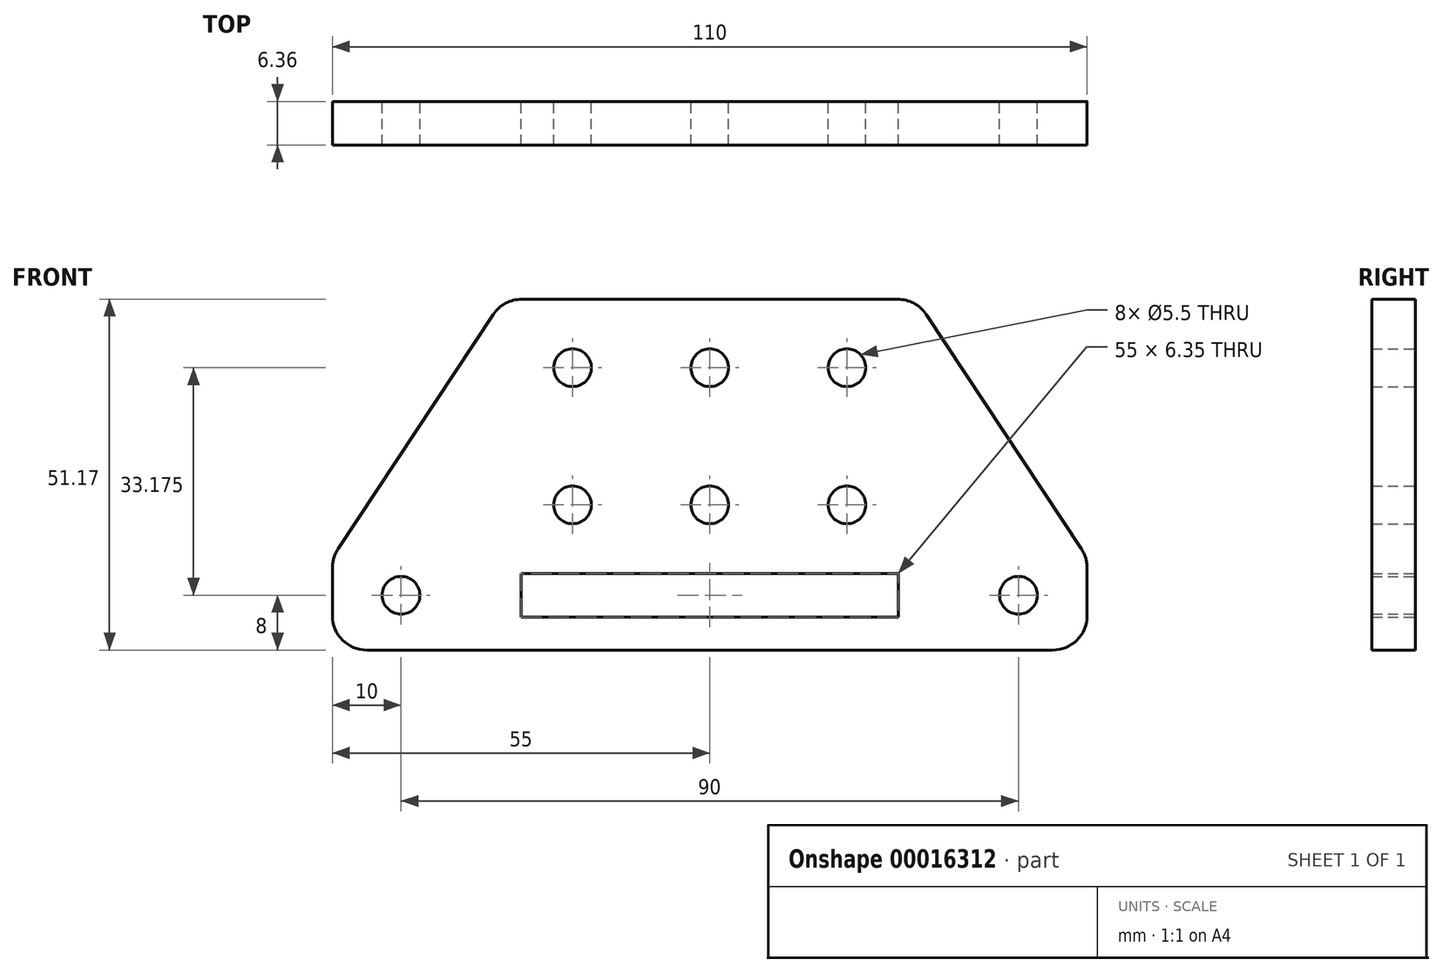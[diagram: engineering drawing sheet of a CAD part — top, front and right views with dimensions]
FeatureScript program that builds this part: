
annotation { "Feature Type Name" : "Feature", "Feature Type Description" : "" }
export const myFeature = defineFeature(function(context is Context, id is Id, definition is map)
    precondition{}
    {
        {
            var Q0;
            Q0=qCreatedBy(makeId("Front.planeOp"),FACE);
            var sketch = newSketch(context, id + "F0", { "sketchPlane" : qUnion([Q0])});
            skLineSegment(sketch, "E0.bottom", {"start": v(-30, 0) * mm, "end": v(30, 0) * mm, "construction": true});
            skLineSegment(sketch, "E0.top", {"start": v(-30, 48.1) * mm, "end": v(30, 48.1) * mm, "construction": true});
            skLineSegment(sketch, "E0.left", {"start": v(-30, 0) * mm, "end": v(-30, 48.1) * mm, "construction": true});
            skLineSegment(sketch, "E0.right", {"start": v(30, 0) * mm, "end": v(30, 48.1) * mm, "construction": true});
            skLineSegment(sketch, "E1", {"start": v(0, 0) * mm, "end": v(0, -10) * mm, "construction": true});
            skLineSegment(sketch, "E2", {"start": v(-55, -3) * mm, "end": v(-55, 4.02) * mm});
            skLineSegment(sketch, "E3", {"start": v(-54.17, 6.78) * mm, "end": v(-31.56, 40.93) * mm});
            skLineSegment(sketch, "E4.MirrorCS", {"start": v(54.17, 6.78) * mm, "end": v(31.56, 40.93) * mm});
            skLineSegment(sketch, "E5.MirrorCS", {"start": v(55, -3) * mm, "end": v(55, 4.02) * mm});
            skLineSegment(sketch, "E6", {"start": v(-27.4, 43.18) * mm, "end": v(27.4, 43.18) * mm});
            skLineSegment(sketch, "E7", {"start": v(-50, -8) * mm, "end": v(50, -8) * mm});
            skCircle(sketch, "E8", {"center": v(-45, 0) * mm, "radius": 2.75 * mm});
            skCircle(sketch, "E9", {"center": v(-20, 33.18) * mm, "radius": 2.75 * mm});
            skCircle(sketch, "E10", {"center": v(-20, 13.18) * mm, "radius": 2.75 * mm});
            skCircle(sketch, "E11", {"center": v(0, 33.18) * mm, "radius": 2.75 * mm});
            skCircle(sketch, "E12", {"center": v(0, 13.18) * mm, "radius": 2.75 * mm});
            skLineSegment(sketch, "E13", {"start": v(0, 33.18) * mm, "end": v(-20, 33.18) * mm, "construction": true});
            skCircle(sketch, "E14.MirrorC", {"center": v(45, 0) * mm, "radius": 2.75 * mm});
            skCircle(sketch, "E15.MirrorC", {"center": v(20, 13.18) * mm, "radius": 2.75 * mm});
            skCircle(sketch, "E16.MirrorC", {"center": v(20, 33.18) * mm, "radius": 2.75 * mm});
            skLineSegment(sketch, "E17", {"start": v(-20, 33.18) * mm, "end": v(-20, 13.18) * mm, "construction": true});
            skLineSegment(sketch, "E18", {"start": v(-20, 33.18) * mm, "end": v(-20, 43.18) * mm, "construction": true});
            skLineSegment(sketch, "E19", {"start": v(-20, 0) * mm, "end": v(-20, -8) * mm, "construction": true});
            skLineSegment(sketch, "E20", {"start": v(-55, 5.52) * mm, "end": v(-55, 43.17) * mm, "construction": true});
            skLineSegment(sketch, "E21", {"start": v(-55, 0) * mm, "end": v(-45, 0) * mm, "construction": true});
            skLineSegment(sketch, "E22", {"start": v(-30, 0) * mm, "end": v(-45, 0) * mm, "construction": true});
            skLineSegment(sketch, "E23", {"start": v(-55, 43.17) * mm, "end": v(-30.08, 43.18) * mm, "construction": true});
            skLineSegment(sketch, "E24", {"start": v(30.08, 43.18) * mm, "end": v(55, 43.18) * mm, "construction": true});
            skLineSegment(sketch, "E25", {"start": v(55, 43.17) * mm, "end": v(55, 5.52) * mm, "construction": true});
            skLineSegment(sketch, "E26.bottom", {"start": v(-27.5, -3.17) * mm, "end": v(27.5, -3.18) * mm});
            skLineSegment(sketch, "E26.top", {"start": v(-27.5, 3.18) * mm, "end": v(27.5, 3.17) * mm});
            skLineSegment(sketch, "E26.left", {"start": v(-27.5, -3.18) * mm, "end": v(-27.5, 3.17) * mm});
            skLineSegment(sketch, "E26.right", {"start": v(27.5, -3.18) * mm, "end": v(27.5, 3.18) * mm});
            skPoint(sketch, "E27", {"position": v(0, -3.18) * mm});
            skPoint(sketch, "E28", {"position": v(27.5, 0) * mm});
            skLineSegment(sketch, "E29", {"start": v(-20, 13.18) * mm, "end": v(-20, 3.18) * mm, "construction": true});
            skPoint(sketch, "E30.visualSharp", {"position": v(-30.08, 43.18) * mm});
            skArc(sketch, "E30.filletArc", {"start": v(-27.4, 43.17) * mm, "mid": v(-29.76, 42.58) * mm, "end": v(-31.56, 40.93) * mm});
            skPoint(sketch, "E31.visualSharp", {"position": v(30.08, 43.18) * mm});
            skArc(sketch, "E31.filletArc", {"start": v(30.04, 43.24) * mm, "mid": v(29.96, 43.24) * mm, "end": v(30, 43.18) * mm});
            skPoint(sketch, "E32.visualSharp", {"position": v(55, 5.52) * mm});
            skArc(sketch, "E32.filletArc", {"start": v(55, 4.02) * mm, "mid": v(54.79, 5.46) * mm, "end": v(54.17, 6.78) * mm});
            skPoint(sketch, "E33.visualSharp", {"position": v(55, -8) * mm});
            skArc(sketch, "E33.filletArc", {"start": v(50, -8) * mm, "mid": v(53.54, -6.54) * mm, "end": v(55, -3) * mm});
            skPoint(sketch, "E34.visualSharp", {"position": v(-55, -8) * mm});
            skArc(sketch, "E34.filletArc", {"start": v(-55, -3) * mm, "mid": v(-53.54, -6.54) * mm, "end": v(-50, -8) * mm});
            skPoint(sketch, "E35.visualSharp", {"position": v(-55, 5.52) * mm});
            skArc(sketch, "E35.filletArc", {"start": v(-54.17, 6.78) * mm, "mid": v(-54.79, 5.46) * mm, "end": v(-55, 4.02) * mm});
            skArc(sketch, "E36.filletArc", {"start": v(31.56, 40.93) * mm, "mid": v(29.76, 42.58) * mm, "end": v(27.4, 43.18) * mm});
            skSolve(sketch);
        }
        {
            var Q0;
            Q0 = qSketchRegion(id + "F0", true);
            extrude(context, id + "F1", {"entities" : qUnion([Q0]), "endBound" : BoundingType.SYMMETRIC, "depth" : 6.35 * mm});
        }
    });
